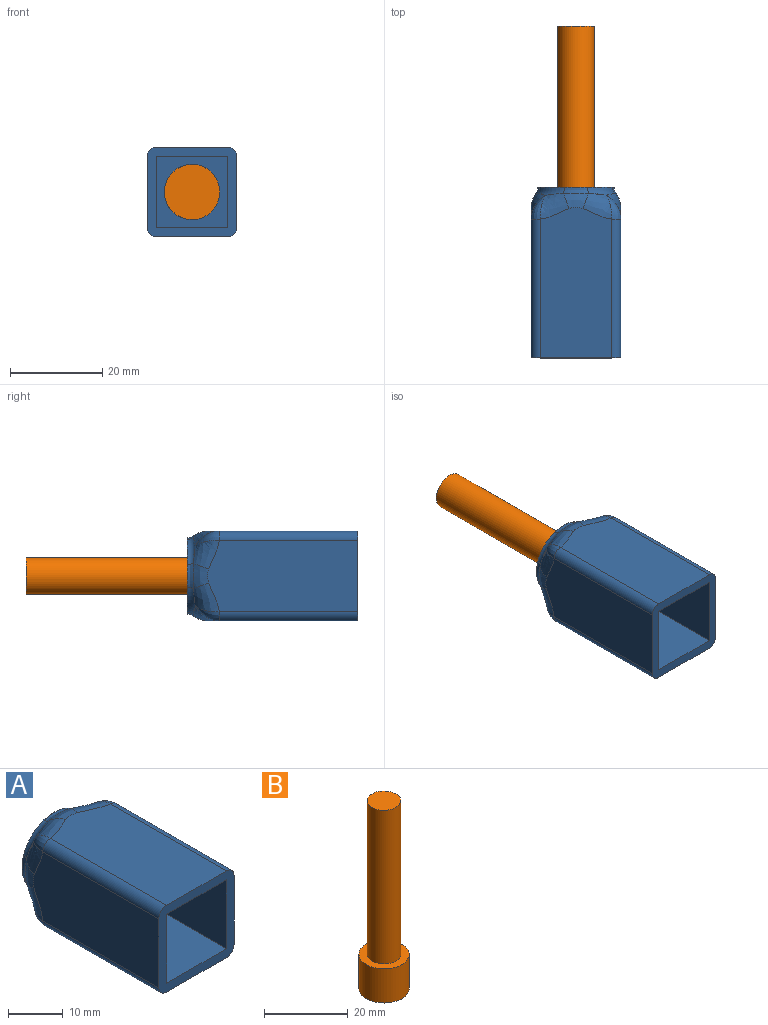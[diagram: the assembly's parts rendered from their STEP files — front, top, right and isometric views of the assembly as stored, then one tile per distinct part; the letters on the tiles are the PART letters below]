
ASSEMBLY  parts=2 mates=1
PART A: 46 faces, bbox 21.1x38.4x21.1 mm
  f0: cylinder r=8.25mm len=5.09mm, axis (0,-1,0), area 0mm2, adj f1,f45
  f1: plane 16.5x16.5mm, normal (0,1,0), area 163.6mm2, adj f0,f2,f38,f39,f40,f41,f42,f43
  f2: cylinder r=4mm len=10mm, axis (0,-1,0), area 251.3mm2, adj f1,f3
  f3: plane 12x12mm, normal (0,-1,0), area 62.8mm2, adj f2,f4
  f4: cylinder r=6mm len=12mm, axis (0,1,0), area 150.8mm2, adj f3,f5
  f5: plane 15.5x15.5mm, normal (0,-1,0), area 127.2mm2, adj f4,f6,f35,f36,f37
  f6: plane 31x15.5mm, normal (1,0,0), area 480.5mm2, adj f5,f7,f35,f37
  f7: plane 19.5x19.5mm, normal (0,-1,0), area 136.6mm2, adj f6,f8,f28,f29,f30,f31,f32,f33
  f8: cylinder r=2mm len=30.1mm, axis (0,-1,0), area 94.6mm2, adj f7,f9,f28,f34
  f9: bspline ~6.33x3.22mm, area 8.7mm2, adj f8,f10,f27
  f10: bspline ~7.51x5.68mm, area 26.4mm2, adj f9,f11,f28,f41
  f11: bspline ~5.4x3.32mm, area 15mm2, adj f10,f12,f13,f28
  f12: bspline ~7.86x2.36mm, area 6.8mm2, adj f11,f39,f40,f41
  f13: bspline ~7.51x5.68mm, area 26.4mm2, adj f11,f14,f28,f39
  f14: bspline ~6.33x3.22mm, area 8.7mm2, adj f13,f15,f29
  f15: bspline ~7.51x5.68mm, area 26.4mm2, adj f14,f16,f30,f39
  f16: bspline ~5.4x3.32mm, area 15mm2, adj f15,f17,f18,f30
  f17: bspline ~7.86x2.36mm, area 6.8mm2, adj f16,f38,f39,f44
  f18: bspline ~7.51x5.68mm, area 26.4mm2, adj f16,f19,f30,f44
  f19: bspline ~6.33x3.22mm, area 8.7mm2, adj f18,f20,f31
  f20: bspline ~7.51x5.68mm, area 26.4mm2, adj f19,f21,f32,f44
  f21: bspline ~5.4x3.32mm, area 15mm2, adj f20,f22,f23,f32
  f22: bspline ~7.86x2.36mm, area 6.8mm2, adj f21,f42,f43,f44
  f23: bspline ~7.51x5.68mm, area 26.4mm2, adj f21,f24,f32,f42
  f24: bspline ~6.33x3.22mm, area 8.7mm2, adj f23,f25,f33
  f25: bspline ~7.51x5.68mm, area 26.4mm2, adj f24,f26,f34,f42
  f26: bspline ~5.4x3.32mm, area 15mm2, adj f25,f27,f34,f45
  f27: bspline ~7.51x5.68mm, area 26.4mm2, adj f9,f26,f34,f41
  f28: plane 32.61x15.51mm, normal (-1,0,0), area 486.3mm2, adj f7,f8,f10,f11,f13,f29
  f29: cylinder r=2mm len=30.1mm, axis (0,1,0), area 94.6mm2, adj f7,f14,f28,f30
  f30: plane 32.61x15.51mm, normal (0,0,1), area 486.3mm2, adj f7,f15,f16,f18,f29,f31
  f31: cylinder r=2mm len=30.1mm, axis (0,-1,0), area 94.6mm2, adj f7,f19,f30,f32
  f32: plane 32.61x15.51mm, normal (1,0,0), area 486.3mm2, adj f7,f20,f21,f23,f31,f33
  f33: cylinder r=2mm len=30.1mm, axis (0,1,0), area 94.6mm2, adj f7,f24,f32,f34
  f34: plane 32.61x15.51mm, normal (0,0,-1), area 486.3mm2, adj f7,f8,f25,f26,f27,f33
  f35: plane 31x15.5mm, normal (0,0,-1), area 480.5mm2, adj f5,f6,f7,f36
  f36: plane 31x15.5mm, normal (-1,0,0), area 480.5mm2, adj f5,f7,f35,f37
  f37: plane 31x15.5mm, normal (0,0,1), area 480.5mm2, adj f5,f6,f7,f36
  f38: cylinder r=8.25mm len=5.09mm, axis (0,-1,0), area 0mm2, adj f1,f17
  f39: torus R=10.25mm, axis (0,-1,0), area 14.2mm2, adj f1,f12,f13,f15,f17
  f40: cylinder r=8.25mm len=5.09mm, axis (0,-1,0), area 0mm2, adj f1,f12
  f41: torus R=10.25mm, axis (0,-1,0), area 14.2mm2, adj f1,f10,f12,f27,f45
  f42: torus R=10.25mm, axis (0,-1,0), area 14.2mm2, adj f1,f22,f23,f25,f45
  f43: cylinder r=8.25mm len=5.09mm, axis (0,-1,0), area 0mm2, adj f1,f22
  f44: torus R=10.25mm, axis (0,-1,0), area 14.2mm2, adj f1,f17,f18,f20,f22
  f45: bspline ~7.86x2.36mm, area 6.8mm2, adj f0,f26,f41,f42
PART B: 5 faces, bbox 12x12x55 mm
  f0: cylinder r=4mm len=45mm, axis (0,0,-1), area 1131mm2, adj f1,f4
  f1: plane 8x8mm, normal (0,0,1), area 50.3mm2, adj f0
  f2: cylinder r=6mm len=12mm, axis (0,0,1), area 377mm2, adj f3,f4
  f3: plane 12x12mm, normal (0,0,-1), area 113.1mm2, adj f2
  f4: plane 12x12mm, normal (0,0,1), area 62.8mm2, adj f0,f2
PLACE A at identity
PLACE B rot(axis=(-1,0,0),90deg) t=(0,-8,0)mm
MATE fastened B.f0 <-> A.f0  axis (0,1,0) through (0,-8,0)mm
